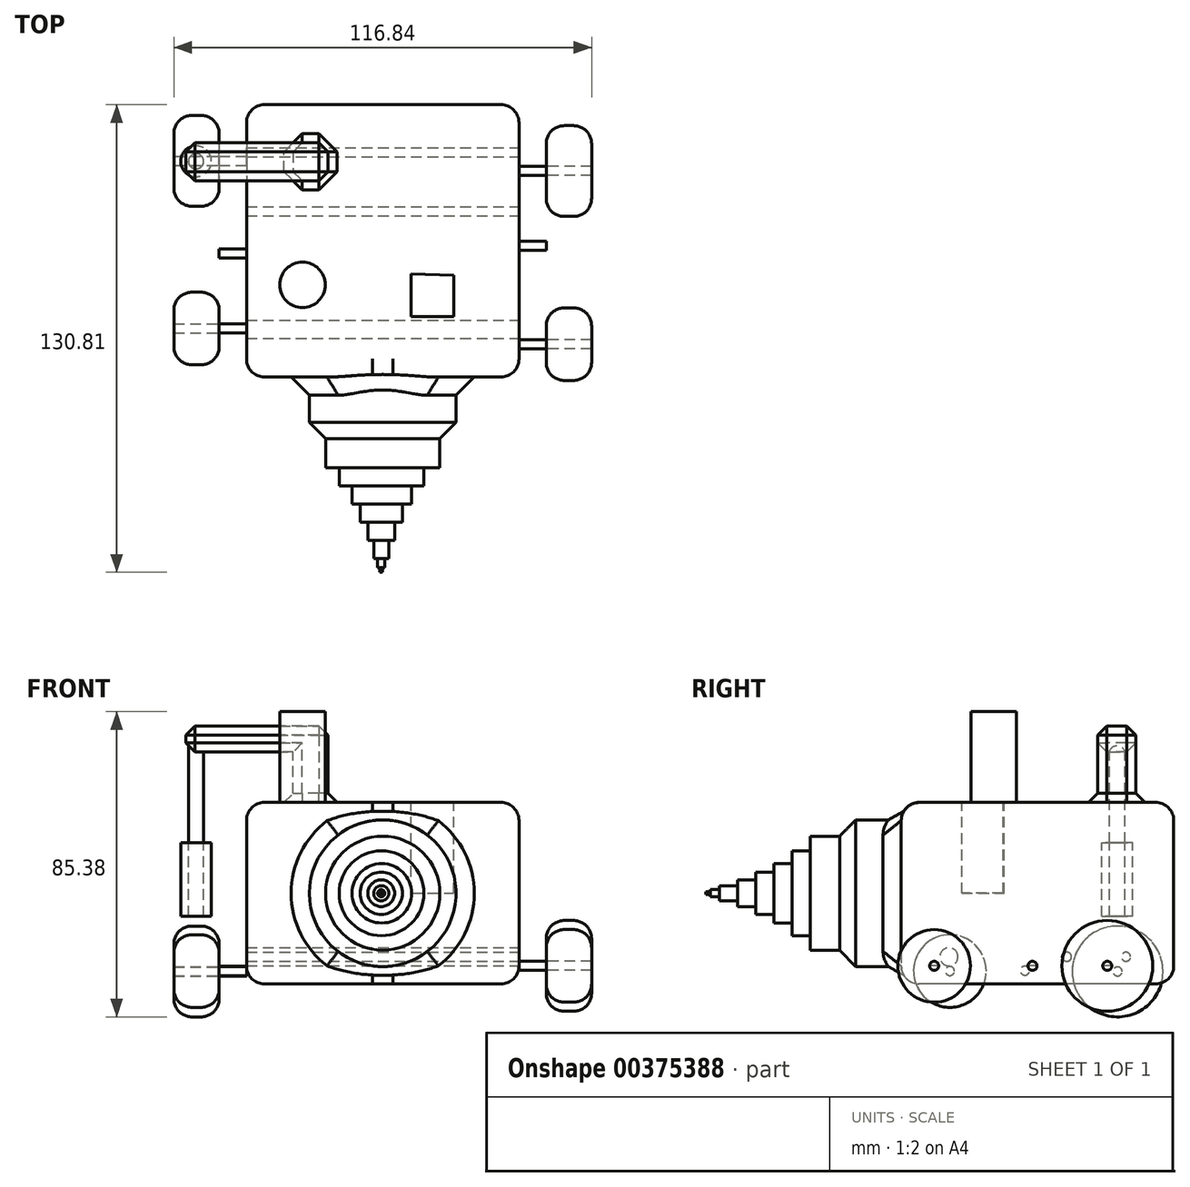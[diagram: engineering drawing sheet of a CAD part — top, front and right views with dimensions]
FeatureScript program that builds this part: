
annotation { "Feature Type Name" : "Feature", "Feature Type Description" : "" }
export const myFeature = defineFeature(function(context is Context, id is Id, definition is map)
    precondition{}
    {
        {
            var Q0;
            Q0=qCreatedBy(makeId("Top.planeOp"),FACE);
            var sketch = newSketch(context, id + "F0", { "sketchPlane" : qUnion([Q0])});
            skLineSegment(sketch, "E0.bottom", {"start": v(-32.92, 41.6) * mm, "end": v(43.28, 41.6) * mm});
            skLineSegment(sketch, "E0.top", {"start": v(-32.92, -34.6) * mm, "end": v(43.28, -34.6) * mm});
            skLineSegment(sketch, "E0.left", {"start": v(-32.92, 41.6) * mm, "end": v(-32.92, -34.6) * mm});
            skLineSegment(sketch, "E0.right", {"start": v(43.28, 41.6) * mm, "end": v(43.28, -34.6) * mm});
            skSolve(sketch);
        }
        {
            var Q0;
            Q0 = qSketchRegion(id + "F0", true);
            extrude(context, id + "F1", {"entities" : qUnion([Q0]), "depth" : 50.8 * mm});
        }
        {
            var Q0;
            Q0=makeQuery(id+"F1.opExtrude","SWEPT_FACE",FACE,{"disambiguationData":[OSD([sQuery(id+"F0.wireOp",EDGE,"E0.top")])]});
            var sketch = newSketch(context, id + "F2", { "sketchPlane" : qUnion([Q0])});
            skCircle(sketch, "E1", {"center": v(5.18, 25.4) * mm, "radius": 20.51 * mm});
            skCircle(sketch, "E2", {"center": v(5.18, 25.4) * mm, "radius": 15.96 * mm});
            skSolve(sketch);
        }
        {
            var Q0;
            Q0=makeQuery(id+"F2.imprint","IMPRINT",FACE,{"disambiguationData":[TD([[makeQuery(id+"F2.imprint","IMPRINT",EDGE,{"derivedFrom":sQuery(id+"F2.wireOp",EDGE,"E1")}),1.0]])]});
            extrude(context, id + "F3", {"entities" : qUnion([Q0]), "operationType" : NewBodyOperationType.ADD, "depth" : 25.4 * mm});
        }
        {
            var Q0;
            Q0=makeQuery(id+"F3.opExtrude","CAP_FACE",FACE,{"disambiguationData":[OSD([sQuery(id+"F2.wireOp",EDGE,"E1"),sQuery(id+"F2.wireOp",EDGE,"E2")])],"isStart":false});
            extrude(context, id + "F4", {"entities" : qUnion([Q0]), "operationType" : NewBodyOperationType.REMOVE, "oppositeDirection" : true, "depth" : 7.62 * mm});
        }
        {
            var Q0;
            Q0=makeQuery(id+"F1.opExtrude","CAP_FACE",FACE,{"disambiguationData":[OSD([sQuery(id+"F0.wireOp",EDGE,"E0.bottom"),sQuery(id+"F0.wireOp",EDGE,"E0.top"),sQuery(id+"F0.wireOp",EDGE,"E0.left"),sQuery(id+"F0.wireOp",EDGE,"E0.right")])],"isStart":false});
            var Q1;
            Q1=makeQuery(id+"F1.opExtrude","SWEPT_FACE",FACE,{"disambiguationData":[OSD([sQuery(id+"F0.wireOp",EDGE,"E0.left")])]});
            var Q2;
            Q2=makeQuery(id+"F1.opExtrude","CAP_FACE",FACE,{"disambiguationData":[OSD([sQuery(id+"F0.wireOp",EDGE,"E0.bottom"),sQuery(id+"F0.wireOp",EDGE,"E0.top"),sQuery(id+"F0.wireOp",EDGE,"E0.left"),sQuery(id+"F0.wireOp",EDGE,"E0.right")])],"isStart":true});
            var Q3;
            Q3=makeQuery(id+"F1.opExtrude","SWEPT_FACE",FACE,{"disambiguationData":[OSD([sQuery(id+"F0.wireOp",EDGE,"E0.bottom")])]});
            var Q4;
            Q4=makeQuery(id+"F1.opExtrude","SWEPT_FACE",FACE,{"disambiguationData":[OSD([sQuery(id+"F0.wireOp",EDGE,"E0.right")])]});
            fillet(context, id + "F5", {"entities" : qUnion([Q0, Q1, Q2, Q3, Q4]), "radius" : 5.08 * mm, "tangentPropagation" : true, "allowEdgeOverflow" : false});
        }
        {
            var Q0;
            Q0=makeQuery(id+"F1.opExtrude","SWEPT_FACE",FACE,{"disambiguationData":[OSD([sQuery(id+"F0.wireOp",EDGE,"E0.left")])]});
            var sketch = newSketch(context, id + "F6", { "sketchPlane" : qUnion([Q0])});
            skSolve(sketch);
        }
        {
            var Q0;
            Q0=makeQuery(id+"F1.opExtrude","SWEPT_FACE",FACE,{"disambiguationData":[OSD([sQuery(id+"F0.wireOp",EDGE,"E0.right")])]});
            var sketch = newSketch(context, id + "F7", { "sketchPlane" : qUnion([Q0])});
            skLineSegment(sketch, "E3", {"start": v(36.53, 10.16) * mm, "end": v(36.53, 5.08) * mm});
            skLineSegment(sketch, "E4", {"start": v(28.27, 5.08) * mm, "end": v(20.02, 5.08) * mm});
            skCircle(sketch, "E5", {"center": v(28.27, 7.62) * mm, "radius": 1.27 * mm});
            skCircle(sketch, "E6", {"center": v(11.76, 7.62) * mm, "radius": 1.27 * mm});
            skCircle(sketch, "E7", {"center": v(-21.26, 7.62) * mm, "radius": 2.54 * mm});
            skSolve(sketch);
        }
        {
            var Q0;
            Q0=makeQuery(id+"F7.imprint","IMPRINT",FACE,{"disambiguationData":[TD([[makeQuery(id+"F7.imprint","IMPRINT",EDGE,{"derivedFrom":sQuery(id+"F7.wireOp",EDGE,"E7")}),1.0]])]});
            var Q1;
            Q1=makeQuery(id+"F7.imprint","IMPRINT",FACE,{"disambiguationData":[TD([[makeQuery(id+"F7.imprint","IMPRINT",EDGE,{"derivedFrom":sQuery(id+"F7.wireOp",EDGE,"E6")}),1.0]])]});
            var Q2;
            Q2=makeQuery(id+"F7.imprint","IMPRINT",FACE,{"disambiguationData":[TD([[makeQuery(id+"F7.imprint","IMPRINT",EDGE,{"derivedFrom":sQuery(id+"F7.wireOp",EDGE,"E5")}),1.0]])]});
            extrude(context, id + "F8", {"entities" : qUnion([Q0, Q1, Q2]), "operationType" : NewBodyOperationType.REMOVE, "endBound" : BoundingType.THROUGH_ALL, "oppositeDirection" : true, "depth" : 25.4 * mm});
        }
        {
            var Q0;
            Q0=makeQuery(id+"F3.boolean.opBoolean","SPLIT",FACE,{"disambiguationData":[TD([makeQuery(id+"F3.opExtrude","SWEPT_FACE",FACE,{"disambiguationData":[OSD([sQuery(id+"F2.wireOp",EDGE,"E2")])]})])],"derivedFrom":makeQuery(id+"F1.opExtrude","SWEPT_FACE",FACE,{"disambiguationData":[OSD([sQuery(id+"F0.wireOp",EDGE,"E0.top")])]})});
            var sketch = newSketch(context, id + "F9", { "sketchPlane" : qUnion([Q0])});
            skCircle(sketch, "E8", {"center": v(5.18, 25.4) * mm, "radius": 12.27 * mm});
            skCircle(sketch, "E9", {"center": v(5.18, 25.4) * mm, "radius": 7.75 * mm});
            skCircle(sketch, "E10", {"center": v(5.18, 25.4) * mm, "radius": 3.83 * mm});
            skCircle(sketch, "E11", {"center": v(5.18, 25.4) * mm, "radius": 1.72 * mm});
            skSolve(sketch);
        }
        {
            var Q0;
            Q0=makeQuery(id+"F9.imprint","IMPRINT",FACE,{"disambiguationData":[TD([[makeQuery(id+"F9.imprint","IMPRINT",EDGE,{"derivedFrom":sQuery(id+"F9.wireOp",EDGE,"E8")}),1.0]])]});
            var Q1;
            Q1=makeQuery(id+"F9.imprint","IMPRINT",FACE,{"disambiguationData":[TD([[makeQuery(id+"F9.imprint","IMPRINT",EDGE,{"derivedFrom":sQuery(id+"F9.wireOp",EDGE,"E8")}),-1.0]])]});
            var Q2;
            Q2=makeQuery(id+"F9.imprint","IMPRINT",FACE,{"disambiguationData":[TD([[makeQuery(id+"F9.imprint","IMPRINT",EDGE,{"derivedFrom":sQuery(id+"F9.wireOp",EDGE,"E9")}),1.0]])]});
            var Q3;
            Q3=makeQuery(id+"F9.imprint","IMPRINT",FACE,{"disambiguationData":[TD([[makeQuery(id+"F9.imprint","IMPRINT",EDGE,{"derivedFrom":sQuery(id+"F9.wireOp",EDGE,"E10")}),1.0]])]});
            var Q4;
            Q4=makeQuery(id+"F9.imprint","IMPRINT",FACE,{"disambiguationData":[TD([[makeQuery(id+"F9.imprint","IMPRINT",EDGE,{"derivedFrom":sQuery(id+"F9.wireOp",EDGE,"E11")}),1.0]])]});
            extrude(context, id + "F10", {"entities" : qUnion([Q0, Q1, Q2, Q3, Q4]), "operationType" : NewBodyOperationType.ADD, "depth" : 25.4 * mm});
        }
        {
            var Q0;
            Q0=makeQuery(id+"F10.opExtrude","CAP_FACE",FACE,{"disambiguationData":[OSD([sQuery(id+"F2.wireOp",EDGE,"E2")])],"isStart":false});
            var sketch = newSketch(context, id + "F11", { "sketchPlane" : qUnion([Q0])});
            skCircle(sketch, "E12", {"center": v(4.86, 25.4) * mm, "radius": 11.86 * mm});
            skSolve(sketch);
        }
        {
            var Q0;
            Q0=makeQuery(id+"F11.imprint","IMPRINT",FACE,{"disambiguationData":[TD([[makeQuery(id+"F11.imprint","IMPRINT",EDGE,{"derivedFrom":sQuery(id+"F11.wireOp",EDGE,"E12")}),1.0]])]});
            extrude(context, id + "F12", {"entities" : qUnion([Q0]), "operationType" : NewBodyOperationType.ADD, "depth" : 5.08 * mm});
        }
        {
            var Q0;
            Q0=makeQuery(id+"F12.opExtrude","CAP_FACE",FACE,{"disambiguationData":[OSD([sQuery(id+"F11.wireOp",EDGE,"E12")])],"isStart":false});
            var sketch = newSketch(context, id + "F13", { "sketchPlane" : qUnion([Q0])});
            skCircle(sketch, "E13", {"center": v(4.92, 25.4) * mm, "radius": 8.32 * mm});
            skSolve(sketch);
        }
        {
            var Q0;
            Q0=makeQuery(id+"F13.imprint","IMPRINT",FACE,{"disambiguationData":[TD([[makeQuery(id+"F13.imprint","IMPRINT",EDGE,{"derivedFrom":sQuery(id+"F13.wireOp",EDGE,"E13")}),1.0]])]});
            extrude(context, id + "F14", {"entities" : qUnion([Q0]), "operationType" : NewBodyOperationType.ADD, "depth" : 5.08 * mm});
        }
        {
            var Q0;
            Q0=makeQuery(id+"F14.opExtrude","CAP_FACE",FACE,{"disambiguationData":[OSD([sQuery(id+"F13.wireOp",EDGE,"E13")])],"isStart":false});
            var sketch = newSketch(context, id + "F15", { "sketchPlane" : qUnion([Q0])});
            skCircle(sketch, "E14", {"center": v(4.77, 25.4) * mm, "radius": 5.92 * mm});
            skSolve(sketch);
        }
        {
            var Q0;
            Q0=makeQuery(id+"F15.imprint","IMPRINT",FACE,{"disambiguationData":[TD([[makeQuery(id+"F15.imprint","IMPRINT",EDGE,{"derivedFrom":sQuery(id+"F15.wireOp",EDGE,"E14")}),1.0]])]});
            extrude(context, id + "F16", {"entities" : qUnion([Q0]), "operationType" : NewBodyOperationType.ADD, "depth" : 5.08 * mm});
        }
        {
            var Q0;
            Q0=makeQuery(id+"F16.opExtrude","CAP_FACE",FACE,{"disambiguationData":[OSD([sQuery(id+"F15.wireOp",EDGE,"E14")])],"isStart":false});
            var sketch = newSketch(context, id + "F17", { "sketchPlane" : qUnion([Q0])});
            skCircle(sketch, "E15", {"center": v(4.77, 25.4) * mm, "radius": 3.74 * mm});
            skSolve(sketch);
        }
        {
            var Q0;
            Q0=makeQuery(id+"F17.imprint","IMPRINT",FACE,{"disambiguationData":[TD([[makeQuery(id+"F17.imprint","IMPRINT",EDGE,{"derivedFrom":sQuery(id+"F17.wireOp",EDGE,"E15")}),1.0]])]});
            extrude(context, id + "F18", {"entities" : qUnion([Q0]), "operationType" : NewBodyOperationType.ADD, "depth" : 5.08 * mm});
        }
        {
            var Q0;
            Q0=makeQuery(id+"F18.opExtrude","CAP_FACE",FACE,{"disambiguationData":[OSD([sQuery(id+"F17.wireOp",EDGE,"E15")])],"isStart":false});
            var sketch = newSketch(context, id + "F19", { "sketchPlane" : qUnion([Q0])});
            skCircle(sketch, "E16", {"center": v(4.77, 25.4) * mm, "radius": 2.12 * mm});
            skSolve(sketch);
        }
        {
            var Q0;
            Q0=makeQuery(id+"F19.imprint","IMPRINT",FACE,{"disambiguationData":[TD([[makeQuery(id+"F19.imprint","IMPRINT",EDGE,{"derivedFrom":sQuery(id+"F19.wireOp",EDGE,"E16")}),1.0]])]});
            extrude(context, id + "F20", {"entities" : qUnion([Q0]), "operationType" : NewBodyOperationType.ADD, "depth" : 5.08 * mm});
        }
        {
            var Q0;
            Q0=makeQuery(id+"F20.opExtrude","CAP_FACE",FACE,{"disambiguationData":[OSD([sQuery(id+"F19.wireOp",EDGE,"E16")])],"isStart":false});
            var sketch = newSketch(context, id + "F21", { "sketchPlane" : qUnion([Q0])});
            skCircle(sketch, "E17", {"center": v(4.77, 25.4) * mm, "radius": 1 * mm});
            skSolve(sketch);
        }
        {
            var Q0;
            Q0=makeQuery(id+"F21.imprint","IMPRINT",FACE,{"disambiguationData":[TD([[makeQuery(id+"F21.imprint","IMPRINT",EDGE,{"derivedFrom":sQuery(id+"F21.wireOp",EDGE,"E17")}),1.0]])]});
            extrude(context, id + "F22", {"entities" : qUnion([Q0]), "operationType" : NewBodyOperationType.ADD, "depth" : 2.54 * mm});
        }
        {
            var Q0;
            Q0=makeQuery(id+"F22.opExtrude","CAP_FACE",FACE,{"disambiguationData":[OSD([sQuery(id+"F21.wireOp",EDGE,"E17")])],"isStart":false});
            var sketch = newSketch(context, id + "F23", { "sketchPlane" : qUnion([Q0])});
            skCircle(sketch, "E18", {"center": v(4.77, 25.4) * mm, "radius": 0.36 * mm});
            skSolve(sketch);
        }
        {
            var Q0;
            Q0=makeQuery(id+"F23.imprint","IMPRINT",FACE,{"disambiguationData":[TD([[makeQuery(id+"F23.imprint","IMPRINT",EDGE,{"derivedFrom":sQuery(id+"F23.wireOp",EDGE,"E18")}),1.0]])]});
            extrude(context, id + "F24", {"entities" : qUnion([Q0]), "operationType" : NewBodyOperationType.ADD, "depth" : 1.27 * mm});
        }
        {
            var Q0;
            Q0=makeQuery(id+"F3.opExtrude","SWEPT_FACE",FACE,{"disambiguationData":[OSD([sQuery(id+"F2.wireOp",EDGE,"E1")])]});
            chamfer(context, id + "F25", {"entities" : qUnion([Q0]), "width" : 5.08 * mm, "tangentPropagation" : true});
        }
        {
            var Q0;
            Q0=makeQuery(id+"F1.opExtrude","CAP_FACE",FACE,{"disambiguationData":[OSD([sQuery(id+"F0.wireOp",EDGE,"E0.bottom"),sQuery(id+"F0.wireOp",EDGE,"E0.top"),sQuery(id+"F0.wireOp",EDGE,"E0.left"),sQuery(id+"F0.wireOp",EDGE,"E0.right")])],"isStart":false});
            var sketch = newSketch(context, id + "F26", { "sketchPlane" : qUnion([Q0])});
            skLineSegment(sketch, "E19", {"start": v(25.03, -6.11) * mm, "end": v(25.03, -17.67) * mm});
            skLineSegment(sketch, "E20", {"start": v(13.15, -17.67) * mm, "end": v(13.15, -5.79) * mm});
            skLineSegment(sketch, "E21", {"start": v(13.15, -5.79) * mm, "end": v(25.03, -6.11) * mm});
            skLineSegment(sketch, "E22", {"start": v(25.03, -17.67) * mm, "end": v(13.15, -17.67) * mm});
            skSolve(sketch);
        }
        {
            var Q0;
            Q0=makeQuery(id+"F26.imprint","IMPRINT",FACE,{"disambiguationData":[TD([[makeQuery(id+"F26.imprint","IMPRINT",EDGE,{"derivedFrom":sQuery(id+"F26.wireOp",EDGE,"E19")}),-1.0]])]});
            extrude(context, id + "F27", {"entities" : qUnion([Q0]), "operationType" : NewBodyOperationType.REMOVE, "oppositeDirection" : true, "depth" : 25.4 * mm});
        }
        {
            var Q0;
            Q0=makeQuery(id+"F1.opExtrude","CAP_FACE",FACE,{"disambiguationData":[OSD([sQuery(id+"F0.wireOp",EDGE,"E0.bottom"),sQuery(id+"F0.wireOp",EDGE,"E0.top"),sQuery(id+"F0.wireOp",EDGE,"E0.left"),sQuery(id+"F0.wireOp",EDGE,"E0.right")])],"isStart":false});
            var sketch = newSketch(context, id + "F28", { "sketchPlane" : qUnion([Q0])});
            skCircle(sketch, "E23", {"center": v(-17.25, -8.79) * mm, "radius": 6.35 * mm});
            skSolve(sketch);
        }
        {
            var Q0;
            Q0=makeQuery(id+"F28.imprint","IMPRINT",FACE,{"disambiguationData":[TD([[makeQuery(id+"F28.imprint","IMPRINT",EDGE,{"derivedFrom":sQuery(id+"F28.wireOp",EDGE,"E23")}),1.0]])]});
            extrude(context, id + "F29", {"entities" : qUnion([Q0]), "operationType" : NewBodyOperationType.ADD, "depth" : 25.4 * mm});
        }
        {
            var Q0;
            {var subQ0=sQuery(id+"F0.wireOp",EDGE,"E0.left");var subQ1=makeQuery(id+"F1.opExtrude","SWEPT_FACE",FACE,{"disambiguationData":[OSD([subQ0])]});Q0=makeQuery(id+"F6.imprint","IMPRINT",FACE,{"disambiguationData":[TD([[makeQuery(id+"F6.imprint","IMPRINT",EDGE,{"derivedFrom":makeQuery(id+"F5.opFillet","BLEND_EDGE",EDGE,{"blendedFrom":[makeQuery(id+"F1.opExtrude","CAP_EDGE",EDGE,{"disambiguationData":[OSD([subQ0])],"isStart":true}),subQ1],"blendedInto":[subQ1]})}),1.0]])]});}
            var sketch = newSketch(context, id + "F30", { "sketchPlane" : qUnion([Q0])});
            skCircle(sketch, "E24", {"center": v(-25.9, 3.52) * mm, "radius": 1.27 * mm});
            skCircle(sketch, "E25", {"center": v(0, 3.75) * mm, "radius": 1.27 * mm});
            skCircle(sketch, "E26", {"center": v(21, 3.64) * mm, "radius": 1.27 * mm});
            skSolve(sketch);
        }
        {
            var Q0;
            Q0=makeQuery(id+"F30.imprint","IMPRINT",FACE,{"disambiguationData":[TD([[makeQuery(id+"F30.imprint","IMPRINT",EDGE,{"derivedFrom":sQuery(id+"F30.wireOp",EDGE,"E24")}),1.0]])]});
            var Q1;
            Q1=makeQuery(id+"F30.imprint","IMPRINT",FACE,{"disambiguationData":[TD([[makeQuery(id+"F30.imprint","IMPRINT",EDGE,{"derivedFrom":sQuery(id+"F30.wireOp",EDGE,"E25")}),1.0]])]});
            var Q2;
            Q2=makeQuery(id+"F30.imprint","IMPRINT",FACE,{"disambiguationData":[TD([[makeQuery(id+"F30.imprint","IMPRINT",EDGE,{"derivedFrom":sQuery(id+"F30.wireOp",EDGE,"E26")}),1.0]])]});
            extrude(context, id + "F31", {"entities" : qUnion([Q0, Q1, Q2]), "depth" : 7.62 * mm});
        }
        {
            var Q0;
            Q0=makeQuery(id+"F1.opExtrude","CAP_FACE",FACE,{"disambiguationData":[OSD([sQuery(id+"F0.wireOp",EDGE,"E0.bottom"),sQuery(id+"F0.wireOp",EDGE,"E0.top"),sQuery(id+"F0.wireOp",EDGE,"E0.left"),sQuery(id+"F0.wireOp",EDGE,"E0.right")])],"isStart":false});
            var sketch = newSketch(context, id + "F32", { "sketchPlane" : qUnion([Q0])});
            skLineSegment(sketch, "E27.bottom", {"start": v(-19.86, 30.96) * mm, "end": v(-10.15, 30.96) * mm});
            skLineSegment(sketch, "E27.top", {"start": v(-19.86, 20.35) * mm, "end": v(-10.15, 20.35) * mm});
            skLineSegment(sketch, "E27.left", {"start": v(-19.86, 30.96) * mm, "end": v(-19.86, 20.35) * mm});
            skLineSegment(sketch, "E27.right", {"start": v(-10.15, 30.96) * mm, "end": v(-10.15, 20.35) * mm});
            skSolve(sketch);
        }
        {
            var Q0;
            Q0=makeQuery(id+"F32.imprint","IMPRINT",FACE,{"disambiguationData":[TD([[makeQuery(id+"F32.imprint","IMPRINT",EDGE,{"derivedFrom":sQuery(id+"F32.wireOp",EDGE,"E27.bottom")}),-1.0]])]});
            extrude(context, id + "F33", {"entities" : qUnion([Q0]), "operationType" : NewBodyOperationType.ADD, "depth" : 25.4 * mm});
        }
        {
            var Q0;
            Q0=makeQuery(id+"F33.opExtrude","SWEPT_FACE",FACE,{"disambiguationData":[OSD([sQuery(id+"F32.wireOp",EDGE,"E27.left")])]});
            var sketch = newSketch(context, id + "F34", { "sketchPlane" : qUnion([Q0])});
            skLineSegment(sketch, "E28.bottom", {"start": v(-30.96, 72.16) * mm, "end": v(-20.35, 72.16) * mm});
            skLineSegment(sketch, "E28.top", {"start": v(-30.96, 64.9) * mm, "end": v(-20.35, 64.9) * mm});
            skLineSegment(sketch, "E28.left", {"start": v(-30.96, 72.16) * mm, "end": v(-30.96, 64.9) * mm});
            skLineSegment(sketch, "E28.right", {"start": v(-20.35, 72.16) * mm, "end": v(-20.35, 64.9) * mm});
            skSolve(sketch);
        }
        {
            var Q0;
            Q0=makeQuery(id+"F34.imprint","IMPRINT",FACE,{"disambiguationData":[TD([[makeQuery(id+"F34.imprint","IMPRINT",EDGE,{"derivedFrom":sQuery(id+"F34.wireOp",EDGE,"E28.bottom")}),-1.0]])]});
            extrude(context, id + "F35", {"entities" : qUnion([Q0]), "operationType" : NewBodyOperationType.ADD, "depth" : 29.97 * mm});
        }
        {
            var Q0;
            {var subQ1=sQuery(id+"F32.wireOp",EDGE,"E27.left");Q0=makeQuery(id+"F35.boolean.opBoolean","SPLIT",FACE,{"disambiguationData":[TD([makeQuery(id+"F35.opExtrude","SWEPT_FACE",FACE,{"disambiguationData":[OSD([sQuery(id+"F34.wireOp",EDGE,"E28.bottom")])]})])],"derivedFrom":makeQuery(id+"F33.opExtrude","SWEPT_FACE",FACE,{"disambiguationData":[OSD([subQ1])]})});}
            extrude(context, id + "F36", {"entities" : qUnion([Q0]), "operationType" : NewBodyOperationType.REMOVE, "endBound" : BoundingType.THROUGH_ALL, "oppositeDirection" : true, "depth" : 25.4 * mm});
        }
        {
            var Q0;
            Q0=makeQuery(id+"F35.opExtrude","SWEPT_FACE",FACE,{"disambiguationData":[OSD([sQuery(id+"F34.wireOp",EDGE,"E28.top")])]});
            var sketch = newSketch(context, id + "F37", { "sketchPlane" : qUnion([Q0])});
            skCircle(sketch, "E29", {"center": v(-47.02, -25.78) * mm, "radius": 2.13 * mm});
            skSolve(sketch);
        }
        {
            var Q0;
            Q0=makeQuery(id+"F37.imprint","IMPRINT",FACE,{"disambiguationData":[TD([[makeQuery(id+"F37.imprint","IMPRINT",EDGE,{"derivedFrom":sQuery(id+"F37.wireOp",EDGE,"E29")}),1.0]])]});
            extrude(context, id + "F38", {"entities" : qUnion([Q0]), "operationType" : NewBodyOperationType.ADD, "depth" : 25.4 * mm});
        }
        {
            var Q0;
            Q0=makeQuery(id+"F38.opExtrude","CAP_FACE",FACE,{"disambiguationData":[OSD([sQuery(id+"F37.wireOp",EDGE,"E29")])],"isStart":false});
            var sketch = newSketch(context, id + "F39", { "sketchPlane" : qUnion([Q0])});
            skCircle(sketch, "E30", {"center": v(-47.02, -25.78) * mm, "radius": 4.3 * mm});
            skSolve(sketch);
        }
        {
            var Q0;
            Q0=makeQuery(id+"F39.imprint","IMPRINT",FACE,{"disambiguationData":[TD([[makeQuery(id+"F39.imprint","IMPRINT",EDGE,{"derivedFrom":sQuery(id+"F39.wireOp",EDGE,"E30")}),1.0]])]});
            extrude(context, id + "F40", {"entities" : qUnion([Q0]), "depth" : 20.57 * mm});
        }
        {
            var Q0;
            Q0=makeQuery(id+"F38.opExtrude","CAP_FACE",FACE,{"disambiguationData":[OSD([sQuery(id+"F37.wireOp",EDGE,"E29")])],"isStart":false});
            var sketch = newSketch(context, id + "F41", { "sketchPlane" : qUnion([Q0])});
            skCircle(sketch, "E31", {"center": v(-47.02, -25.78) * mm, "radius": 4.22 * mm});
            skSolve(sketch);
        }
        {
            var Q0;
            Q0=makeQuery(id+"F35.boolean.opBoolean","MERGE",FACE,{"derivedFrom":[makeQuery(id+"F33.opExtrude","SWEPT_FACE",FACE,{"disambiguationData":[OSD([sQuery(id+"F32.wireOp",EDGE,"E27.bottom")])]}),makeQuery(id+"F35.opExtrude","SWEPT_FACE",FACE,{"disambiguationData":[OSD([sQuery(id+"F34.wireOp",EDGE,"E28.left")])]})]});
            var Q1;
            Q1=makeQuery(id+"F35.opExtrude","CAP_FACE",FACE,{"disambiguationData":[OSD([sQuery(id+"F34.wireOp",EDGE,"E28.bottom"),sQuery(id+"F34.wireOp",EDGE,"E28.top"),sQuery(id+"F34.wireOp",EDGE,"E28.left"),sQuery(id+"F34.wireOp",EDGE,"E28.right")])],"isStart":false});
            var Q2;
            Q2=makeQuery(id+"F33.opExtrude","SWEPT_FACE",FACE,{"disambiguationData":[OSD([sQuery(id+"F32.wireOp",EDGE,"E27.right")])]});
            var Q3;
            Q3=makeQuery(id+"F35.boolean.opBoolean","MERGE",FACE,{"derivedFrom":[makeQuery(id+"F33.opExtrude","SWEPT_FACE",FACE,{"disambiguationData":[OSD([sQuery(id+"F32.wireOp",EDGE,"E27.top")])]}),makeQuery(id+"F35.opExtrude","SWEPT_FACE",FACE,{"disambiguationData":[OSD([sQuery(id+"F34.wireOp",EDGE,"E28.right")])]})]});
            chamfer(context, id + "F42", {"entities" : qUnion([Q0, Q1, Q2, Q3]), "width" : 2.54 * mm, "tangentPropagation" : true});
        }
        {
            var Q0;
            Q0=makeQuery(id+"F1.opExtrude","SWEPT_FACE",FACE,{"disambiguationData":[OSD([sQuery(id+"F0.wireOp",EDGE,"E0.right")])]});
            var sketch = newSketch(context, id + "F43", { "sketchPlane" : qUnion([Q0])});
            skCircle(sketch, "E32", {"center": v(-25.39, 5.08) * mm, "radius": 1.27 * mm});
            skCircle(sketch, "E33", {"center": v(2.1, 5.08) * mm, "radius": 1.27 * mm});
            skCircle(sketch, "E34", {"center": v(23.04, 5.08) * mm, "radius": 1.27 * mm});
            skSolve(sketch);
        }
        {
            var Q0;
            {var subQ0=sQuery(id+"F43.wireOp",EDGE,"E32");var subQ1=sQuery(id+"F0.wireOp",EDGE,"E0.right");var subQ2=makeQuery(id+"F1.opExtrude","CAP_EDGE",EDGE,{"disambiguationData":[OSD([subQ1])],"isStart":true});var subQ3=sQuery(id+"F0.wireOp",EDGE,"E0.top");var subQ4=makeQuery(id+"F1.opExtrude","SWEPT_FACE",FACE,{"disambiguationData":[OSD([subQ1])]});var subQ5=makeQuery(id+"F8.boolean.opBoolean","SPLIT",EDGE,{"disambiguationData":[TD([makeQuery(id+"F5.opFillet","BLEND_FACE",FACE,{"disambiguationData":[OSD([subQ3,subQ1]),TDD([makeQuery(id+"F1.opExtrude","CAP_VERTEX",VERTEX,{"disambiguationData":[OSD([subQ3,subQ1])],"isStart":true})])]})])],"derivedFrom":makeQuery(id+"F5.opFillet","BLEND_EDGE",EDGE,{"blendedFrom":[subQ2,subQ4],"blendedInto":[subQ4]})});var subQ6=makeQuery(id+"F43.imprint","INTERSECT",VERTEX,{"disambiguationData":[OD(0.0)],"derivedFrom":[subQ5,subQ0]});Q0=makeQuery(id+"F43.imprint","IMPRINT",FACE,{"disambiguationData":[TD([[makeQuery(id+"F43.imprint","IMPRINT",EDGE,{"disambiguationData":[TD([[subQ6,-1.0]])],"derivedFrom":subQ0}),1.0]])]});}
            var Q1;
            {var subQ0=sQuery(id+"F43.wireOp",EDGE,"E32");var subQ1=sQuery(id+"F0.wireOp",EDGE,"E0.right");var subQ2=makeQuery(id+"F1.opExtrude","CAP_EDGE",EDGE,{"disambiguationData":[OSD([subQ1])],"isStart":true});var subQ3=sQuery(id+"F0.wireOp",EDGE,"E0.top");var subQ4=makeQuery(id+"F1.opExtrude","SWEPT_FACE",FACE,{"disambiguationData":[OSD([subQ1])]});var subQ5=makeQuery(id+"F8.boolean.opBoolean","SPLIT",EDGE,{"disambiguationData":[TD([makeQuery(id+"F5.opFillet","BLEND_FACE",FACE,{"disambiguationData":[OSD([subQ3,subQ1]),TDD([makeQuery(id+"F1.opExtrude","CAP_VERTEX",VERTEX,{"disambiguationData":[OSD([subQ3,subQ1])],"isStart":true})])]})])],"derivedFrom":makeQuery(id+"F5.opFillet","BLEND_EDGE",EDGE,{"blendedFrom":[subQ2,subQ4],"blendedInto":[subQ4]})});var subQ6=makeQuery(id+"F43.imprint","INTERSECT",VERTEX,{"disambiguationData":[OD(0.0)],"derivedFrom":[subQ5,subQ0]});Q1=makeQuery(id+"F43.imprint","IMPRINT",FACE,{"disambiguationData":[TD([[makeQuery(id+"F43.imprint","IMPRINT",EDGE,{"disambiguationData":[TD([[subQ6,1.0]])],"derivedFrom":subQ0}),1.0]])]});}
            var Q2;
            {var subQ0=sQuery(id+"F43.wireOp",EDGE,"E33");var subQ1=sQuery(id+"F0.wireOp",EDGE,"E0.right");var subQ2=makeQuery(id+"F1.opExtrude","CAP_EDGE",EDGE,{"disambiguationData":[OSD([subQ1])],"isStart":true});var subQ3=sQuery(id+"F0.wireOp",EDGE,"E0.bottom");var subQ4=makeQuery(id+"F1.opExtrude","SWEPT_FACE",FACE,{"disambiguationData":[OSD([subQ1])]});var subQ5=makeQuery(id+"F8.boolean.opBoolean","SPLIT",EDGE,{"disambiguationData":[TD([makeQuery(id+"F5.opFillet","BLEND_FACE",FACE,{"disambiguationData":[OSD([subQ3,subQ1]),TDD([makeQuery(id+"F1.opExtrude","CAP_VERTEX",VERTEX,{"disambiguationData":[OSD([subQ3,subQ1])],"isStart":true})])]})])],"derivedFrom":makeQuery(id+"F5.opFillet","BLEND_EDGE",EDGE,{"blendedFrom":[subQ2,subQ4],"blendedInto":[subQ4]})});var subQ6=makeQuery(id+"F43.imprint","INTERSECT",VERTEX,{"disambiguationData":[OD(0.0)],"derivedFrom":[subQ5,subQ0]});Q2=makeQuery(id+"F43.imprint","IMPRINT",FACE,{"disambiguationData":[TD([[makeQuery(id+"F43.imprint","IMPRINT",EDGE,{"disambiguationData":[TD([[subQ6,1.0]])],"derivedFrom":subQ0}),1.0]])]});}
            var Q3;
            {var subQ0=sQuery(id+"F43.wireOp",EDGE,"E33");var subQ1=sQuery(id+"F0.wireOp",EDGE,"E0.right");var subQ2=makeQuery(id+"F1.opExtrude","CAP_EDGE",EDGE,{"disambiguationData":[OSD([subQ1])],"isStart":true});var subQ3=sQuery(id+"F0.wireOp",EDGE,"E0.bottom");var subQ4=makeQuery(id+"F1.opExtrude","SWEPT_FACE",FACE,{"disambiguationData":[OSD([subQ1])]});var subQ5=makeQuery(id+"F8.boolean.opBoolean","SPLIT",EDGE,{"disambiguationData":[TD([makeQuery(id+"F5.opFillet","BLEND_FACE",FACE,{"disambiguationData":[OSD([subQ3,subQ1]),TDD([makeQuery(id+"F1.opExtrude","CAP_VERTEX",VERTEX,{"disambiguationData":[OSD([subQ3,subQ1])],"isStart":true})])]})])],"derivedFrom":makeQuery(id+"F5.opFillet","BLEND_EDGE",EDGE,{"blendedFrom":[subQ2,subQ4],"blendedInto":[subQ4]})});var subQ6=makeQuery(id+"F43.imprint","INTERSECT",VERTEX,{"disambiguationData":[OD(0.0)],"derivedFrom":[subQ5,subQ0]});Q3=makeQuery(id+"F43.imprint","IMPRINT",FACE,{"disambiguationData":[TD([[makeQuery(id+"F43.imprint","IMPRINT",EDGE,{"disambiguationData":[TD([[subQ6,-1.0]])],"derivedFrom":subQ0}),1.0]])]});}
            var Q4;
            {var subQ0=sQuery(id+"F43.wireOp",EDGE,"E34");var subQ1=sQuery(id+"F0.wireOp",EDGE,"E0.right");var subQ2=makeQuery(id+"F1.opExtrude","CAP_EDGE",EDGE,{"disambiguationData":[OSD([subQ1])],"isStart":true});var subQ3=sQuery(id+"F0.wireOp",EDGE,"E0.bottom");var subQ4=makeQuery(id+"F1.opExtrude","SWEPT_FACE",FACE,{"disambiguationData":[OSD([subQ1])]});var subQ5=makeQuery(id+"F8.boolean.opBoolean","SPLIT",EDGE,{"disambiguationData":[TD([makeQuery(id+"F5.opFillet","BLEND_FACE",FACE,{"disambiguationData":[OSD([subQ3,subQ1]),TDD([makeQuery(id+"F1.opExtrude","CAP_VERTEX",VERTEX,{"disambiguationData":[OSD([subQ3,subQ1])],"isStart":true})])]})])],"derivedFrom":makeQuery(id+"F5.opFillet","BLEND_EDGE",EDGE,{"blendedFrom":[subQ2,subQ4],"blendedInto":[subQ4]})});var subQ6=makeQuery(id+"F43.imprint","INTERSECT",VERTEX,{"disambiguationData":[OD(0.0)],"derivedFrom":[subQ5,subQ0]});Q4=makeQuery(id+"F43.imprint","IMPRINT",FACE,{"disambiguationData":[TD([[makeQuery(id+"F43.imprint","IMPRINT",EDGE,{"disambiguationData":[TD([[subQ6,-1.0]])],"derivedFrom":subQ0}),1.0]])]});}
            var Q5;
            {var subQ0=sQuery(id+"F43.wireOp",EDGE,"E34");var subQ1=sQuery(id+"F0.wireOp",EDGE,"E0.right");var subQ2=makeQuery(id+"F1.opExtrude","CAP_EDGE",EDGE,{"disambiguationData":[OSD([subQ1])],"isStart":true});var subQ3=sQuery(id+"F0.wireOp",EDGE,"E0.bottom");var subQ4=makeQuery(id+"F1.opExtrude","SWEPT_FACE",FACE,{"disambiguationData":[OSD([subQ1])]});var subQ5=makeQuery(id+"F8.boolean.opBoolean","SPLIT",EDGE,{"disambiguationData":[TD([makeQuery(id+"F5.opFillet","BLEND_FACE",FACE,{"disambiguationData":[OSD([subQ3,subQ1]),TDD([makeQuery(id+"F1.opExtrude","CAP_VERTEX",VERTEX,{"disambiguationData":[OSD([subQ3,subQ1])],"isStart":true})])]})])],"derivedFrom":makeQuery(id+"F5.opFillet","BLEND_EDGE",EDGE,{"blendedFrom":[subQ2,subQ4],"blendedInto":[subQ4]})});var subQ6=makeQuery(id+"F43.imprint","INTERSECT",VERTEX,{"disambiguationData":[OD(0.0)],"derivedFrom":[subQ5,subQ0]});Q5=makeQuery(id+"F43.imprint","IMPRINT",FACE,{"disambiguationData":[TD([[makeQuery(id+"F43.imprint","IMPRINT",EDGE,{"disambiguationData":[TD([[subQ6,1.0]])],"derivedFrom":subQ0}),1.0]])]});}
            extrude(context, id + "F44", {"entities" : qUnion([Q0, Q1, Q2, Q3, Q4, Q5]), "operationType" : NewBodyOperationType.ADD, "depth" : 7.62 * mm});
        }
        {
            var Q0;
            Q0=makeQuery(id+"F44.opExtrude","CAP_FACE",FACE,{"disambiguationData":[OSD([sQuery(id+"F43.wireOp",EDGE,"E32")])],"isStart":false});
            var sketch = newSketch(context, id + "F45", { "sketchPlane" : qUnion([Q0])});
            skCircle(sketch, "E35", {"center": v(-25.39, 5.08) * mm, "radius": 10.16 * mm});
            skSolve(sketch);
        }
        {
            var Q0;
            Q0=makeQuery(id+"F45.imprint","IMPRINT",FACE,{"disambiguationData":[TD([[makeQuery(id+"F45.imprint","IMPRINT",EDGE,{"derivedFrom":sQuery(id+"F45.wireOp",EDGE,"E35")}),1.0]])]});
            extrude(context, id + "F46", {"entities" : qUnion([Q0]), "depth" : 12.7 * mm});
        }
        {
            var Q0;
            Q0=makeQuery(id+"F31.opExtrude","CAP_FACE",FACE,{"disambiguationData":[OSD([sQuery(id+"F30.wireOp",EDGE,"E26")])],"isStart":false});
            var sketch = newSketch(context, id + "F47", { "sketchPlane" : qUnion([Q0])});
            skCircle(sketch, "E36", {"center": v(21, 3.64) * mm, "radius": 10.16 * mm});
            skSolve(sketch);
        }
        {
            var Q0;
            Q0=makeQuery(id+"F47.imprint","IMPRINT",FACE,{"disambiguationData":[TD([[makeQuery(id+"F47.imprint","IMPRINT",EDGE,{"derivedFrom":sQuery(id+"F47.wireOp",EDGE,"E36")}),1.0]])]});
            extrude(context, id + "F48", {"entities" : qUnion([Q0]), "depth" : 12.7 * mm});
        }
        {
            var Q0;
            Q0=makeQuery(id+"F31.opExtrude","CAP_FACE",FACE,{"disambiguationData":[OSD([sQuery(id+"F30.wireOp",EDGE,"E24")])],"isStart":false});
            var sketch = newSketch(context, id + "F49", { "sketchPlane" : qUnion([Q0])});
            skCircle(sketch, "E37", {"center": v(-25.9, 3.52) * mm, "radius": 12.7 * mm});
            skSolve(sketch);
        }
        {
            var Q0;
            Q0=makeQuery(id+"F49.imprint","IMPRINT",FACE,{"disambiguationData":[TD([[makeQuery(id+"F49.imprint","IMPRINT",EDGE,{"derivedFrom":sQuery(id+"F49.wireOp",EDGE,"E37")}),1.0]])]});
            extrude(context, id + "F50", {"entities" : qUnion([Q0]), "depth" : 12.7 * mm});
        }
        {
            var Q0;
            Q0=makeQuery(id+"F44.opExtrude","CAP_FACE",FACE,{"disambiguationData":[OSD([sQuery(id+"F43.wireOp",EDGE,"E34")])],"isStart":false});
            var sketch = newSketch(context, id + "F51", { "sketchPlane" : qUnion([Q0])});
            skCircle(sketch, "E38", {"center": v(23.04, 5.08) * mm, "radius": 12.7 * mm});
            skSolve(sketch);
        }
        {
            var Q0;
            Q0=makeQuery(id+"F51.imprint","IMPRINT",FACE,{"disambiguationData":[TD([[makeQuery(id+"F51.imprint","IMPRINT",EDGE,{"derivedFrom":sQuery(id+"F51.wireOp",EDGE,"E38")}),1.0]])]});
            extrude(context, id + "F52", {"entities" : qUnion([Q0]), "depth" : 12.7 * mm});
        }
        {
            var Q0;
            Q0=makeQuery(id+"F46.opExtrude","SWEPT_FACE",FACE,{"disambiguationData":[OSD([sQuery(id+"F45.wireOp",EDGE,"E35")])]});
            var Q1;
            Q1=makeQuery(id+"F52.opExtrude","SWEPT_FACE",FACE,{"disambiguationData":[OSD([sQuery(id+"F51.wireOp",EDGE,"E38")])]});
            var Q2;
            Q2=makeQuery(id+"F48.opExtrude","SWEPT_FACE",FACE,{"disambiguationData":[OSD([sQuery(id+"F47.wireOp",EDGE,"E36")])]});
            var Q3;
            Q3=makeQuery(id+"F50.opExtrude","SWEPT_FACE",FACE,{"disambiguationData":[OSD([sQuery(id+"F49.wireOp",EDGE,"E37")])]});
            fillet(context, id + "F53", {"entities" : qUnion([Q0, Q1, Q2, Q3]), "radius" : 5.08 * mm, "tangentPropagation" : true, "allowEdgeOverflow" : false});
        }
    });
